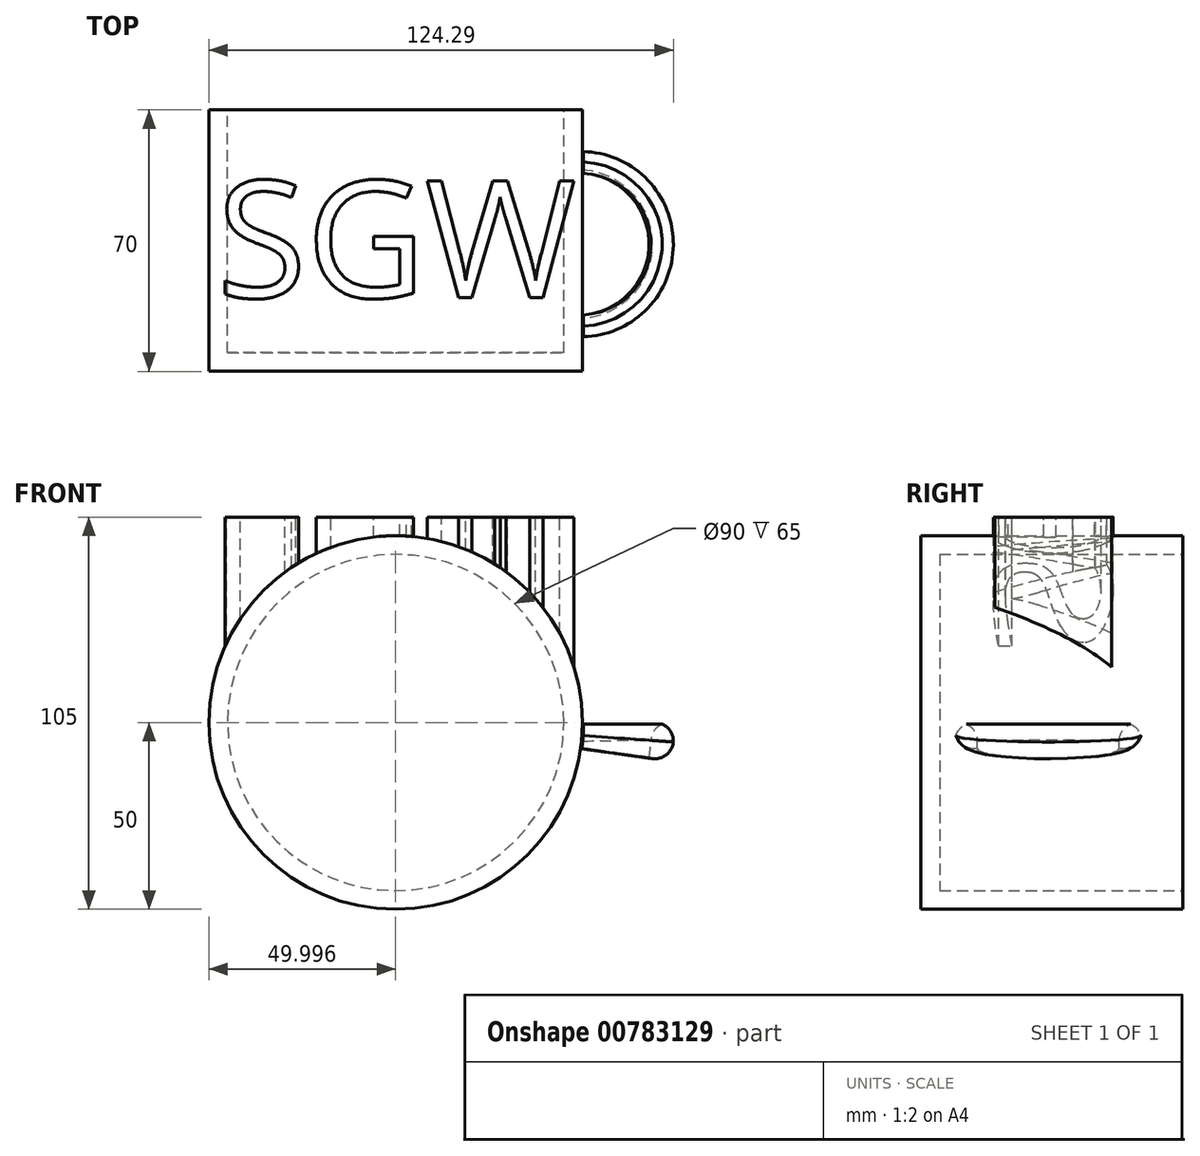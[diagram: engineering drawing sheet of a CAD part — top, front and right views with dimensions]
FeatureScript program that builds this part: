
annotation { "Feature Type Name" : "Feature", "Feature Type Description" : "" }
export const myFeature = defineFeature(function(context is Context, id is Id, definition is map)
    precondition{}
    {
        {
            var Q0;
            Q0=qCreatedBy(makeId("Top.planeOp"),FACE);
            var sketch = newSketch(context, id + "F0", { "sketchPlane" : qUnion([Q0])});
            skLineSegment(sketch, "E0.bottom", {"start": v(-64, 35.92) * mm, "end": v(-59, 35.92) * mm});
            skLineSegment(sketch, "E0.top", {"start": v(-64, -34.08) * mm, "end": v(-14, -34.08) * mm});
            skLineSegment(sketch, "E0.left", {"start": v(-64, 35.92) * mm, "end": v(-64, -34.08) * mm});
            skLineSegment(sketch, "E1", {"start": v(-14, -29.08) * mm, "end": v(-14, -34.08) * mm});
            skLineSegment(sketch, "E2", {"start": v(-59, 35.92) * mm, "end": v(-59, -29.08) * mm});
            skLineSegment(sketch, "E3", {"start": v(-59, -29.08) * mm, "end": v(-14, -29.08) * mm});
            skSolve(sketch);
        }
        {
            var Q0;
            Q0=makeQuery(id+"F0.imprint","IMPRINT",FACE,{"disambiguationData":[TD([[makeQuery(id+"F0.imprint","IMPRINT",EDGE,{"derivedFrom":sQuery(id+"F0.wireOp",EDGE,"E0.bottom")}),-1.0]])]});
            var Q1;
            Q1=sQuery(id+"F0.wireOp",EDGE,"E1");
            revolve(context, id + "F1", {"surfaceOperationType" : NewSurfaceOperationType.NEW, "entities" : qUnion([Q0]), "axis" : qUnion([Q1]), "revolveType" : RevolveType.FULL});
        }
        {
            var Q0;
            Q0=qCreatedBy(makeId("Top.planeOp"),FACE);
            var sketch = newSketch(context, id + "F2", { "sketchPlane" : qUnion([Q0])});
            skArc(sketch, "E4", {"start": v(36.28, -24.99) * mm, "mid": v(60.47, 0) * mm, "end": v(36.28, 24.99) * mm});
            skArc(sketch, "E5", {"start": v(36.28, -18.98) * mm, "mid": v(54.47, 0) * mm, "end": v(36.28, 18.98) * mm});
            skLineSegment(sketch, "E6", {"start": v(36.28, 24.99) * mm, "end": v(36.28, 18.98) * mm});
            skLineSegment(sketch, "E7.trimOffspring", {"start": v(36.28, -18.98) * mm, "end": v(36.28, -24.99) * mm});
            skSolve(sketch);
        }
        {
            var Q0;
            Q0=makeQuery(id+"F2.imprint","IMPRINT",FACE,{"disambiguationData":[TD([[makeQuery(id+"F2.imprint","IMPRINT",EDGE,{"derivedFrom":sQuery(id+"F2.wireOp",EDGE,"E4")}),1.0]])]});
            var Q1;
            Q1=makeQuery(id+"F1.opRevolve","SWEPT_FACE",FACE,{"disambiguationData":[OSD([sQuery(id+"F0.wireOp",EDGE,"E0.left")])]});
            revolve(context, id + "F3", {"surfaceOperationType" : NewSurfaceOperationType.NEW, "entities" : qUnion([Q0]), "axis" : qUnion([Q1]), "revolveType" : RevolveType.ONE_DIRECTION, "angle" : 8 * degree});
        }
        {
            var Q0;
            Q0=qCreatedBy(makeId("Top.planeOp"),FACE);
            cPlane(context, id + "F4", {"entities" : qUnion([Q0]), "cplaneType" : CPlaneType.OFFSET, "offset" : 55 * mm, "width" : 150 * mm, "height" : 150 * mm});
        }
        {
            var Q0;
            Q0=qCreatedBy(id+"F4.planeOp",FACE);
            var sketch = newSketch(context, id + "F5", { "sketchPlane" : qUnion([Q0])});
            skText(sketch, "E8", { "text": "SGW", "fontName": "OpenSans-Regular.ttf"});
            const initialGuessF5  = {"E8": [-0.06188, -0.0143, 1, 0, 0.03145]};
            skSetInitialGuess(sketch, initialGuessF5);
            skSolve(sketch);
        }
        {
            var Q0;
            Q0 = qSketchRegion(id + "F5", true);
            extrude(context, id + "F6", {"entities" : qUnion([Q0]), "operationType" : NewBodyOperationType.ADD, "endBound" : BoundingType.UP_TO_NEXT, "oppositeDirection" : true, "depth" : 25 * mm, "offsetDistance" : 25 * mm});
        }
        {
            var Q0;
            Q0=makeQuery(id+"F3.opRevolve","CAP_EDGE",EDGE,{"disambiguationData":[OSD([sQuery(id+"F2.wireOp",EDGE,"E4")])],"isStart":true});
            var Q1;
            Q1=makeQuery(id+"F3.opRevolve","CAP_EDGE",EDGE,{"disambiguationData":[OSD([sQuery(id+"F2.wireOp",EDGE,"E4")])],"isStart":false});
            var Q2;
            Q2=makeQuery(id+"F3.opRevolve","CAP_EDGE",EDGE,{"disambiguationData":[OSD([sQuery(id+"F2.wireOp",EDGE,"E5")])],"isStart":true});
            fillet(context, id + "F7", {"entities" : qUnion([Q0, Q1, Q2]), "radius" : 5 * mm, "tangentPropagation" : true, "allowEdgeOverflow" : false});
        }
    });
